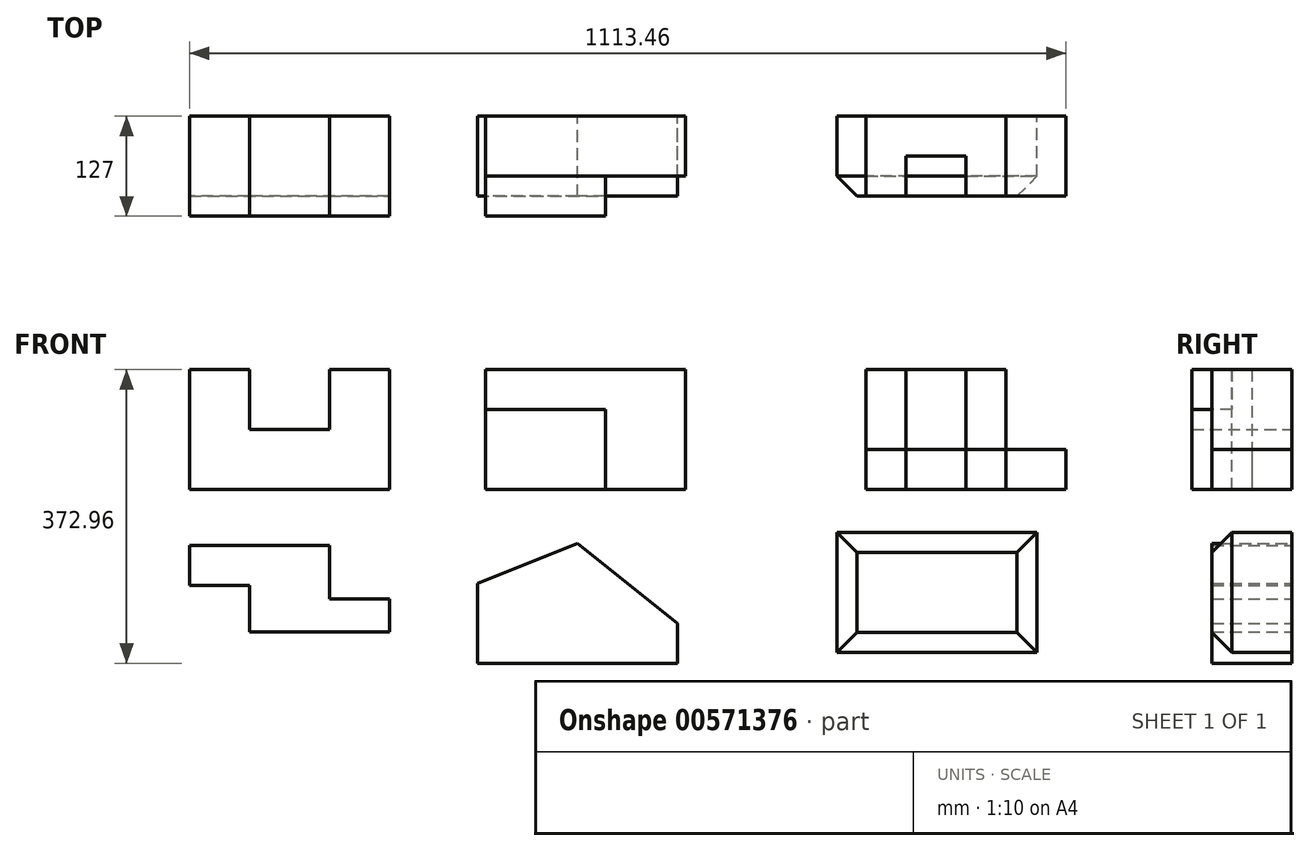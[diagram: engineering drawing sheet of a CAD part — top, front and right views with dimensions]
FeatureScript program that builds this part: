
annotation { "Feature Type Name" : "Feature", "Feature Type Description" : "" }
export const myFeature = defineFeature(function(context is Context, id is Id, definition is map)
    precondition{}
    {
        {
            var Q0;
            Q0=qCreatedBy(makeId("Front.planeOp"),FACE);
            var sketch = newSketch(context, id + "F0", { "sketchPlane" : qUnion([Q0])});
            skLineSegment(sketch, "E0", {"start": v(0, 0) * mm, "end": v(254, 0) * mm});
            skLineSegment(sketch, "E1", {"start": v(254, 0) * mm, "end": v(254, 152.4) * mm});
            skLineSegment(sketch, "E2", {"start": v(254, 152.4) * mm, "end": v(177.8, 152.4) * mm});
            skLineSegment(sketch, "E3", {"start": v(177.8, 152.4) * mm, "end": v(177.8, 76.2) * mm});
            skLineSegment(sketch, "E4", {"start": v(177.8, 76.2) * mm, "end": v(76.2, 76.2) * mm});
            skLineSegment(sketch, "E5", {"start": v(76.2, 76.2) * mm, "end": v(76.2, 152.4) * mm});
            skLineSegment(sketch, "E6", {"start": v(76.2, 152.4) * mm, "end": v(0, 152.4) * mm});
            skLineSegment(sketch, "E7", {"start": v(0, 152.4) * mm, "end": v(0, 0) * mm});
            skSolve(sketch);
        }
        {
            var Q0;
            Q0=makeQuery(id+"F0.imprint","IMPRINT",FACE,{"disambiguationData":[TD([[makeQuery(id+"F0.imprint","IMPRINT",EDGE,{"derivedFrom":sQuery(id+"F0.wireOp",EDGE,"E0")}),1.0]])]});
            var sketch = newSketch(context, id + "F1", { "sketchPlane" : qUnion([Q0])});
            skSolve(sketch);
        }
        {
            var Q0;
            Q0=makeQuery(id+"F1.imprint","IMPRINT",FACE,{"disambiguationData":[TD([[makeQuery(id+"F1.imprint","IMPRINT",EDGE,{"derivedFrom":makeQuery(id+"F0.imprint","IMPRINT",EDGE,{"derivedFrom":sQuery(id+"F0.wireOp",EDGE,"E0")})}),1.0]])]});
            extrude(context, id + "F2", {"entities" : qUnion([Q0]), "depth" : 25.4 * mm, "offsetDistance" : 25.4 * mm});
        }
        {
            var Q0;
            Q0=qCreatedBy(makeId("Front.planeOp"),FACE);
            var sketch = newSketch(context, id + "F3", { "sketchPlane" : qUnion([Q0])});
            skLineSegment(sketch, "E8", {"start": v(376.13, 0) * mm, "end": v(630.13, 0) * mm});
            skLineSegment(sketch, "E9", {"start": v(630.13, 0) * mm, "end": v(630.13, 152.4) * mm});
            skLineSegment(sketch, "E10", {"start": v(630.13, 152.4) * mm, "end": v(376.13, 152.4) * mm});
            skLineSegment(sketch, "E11", {"start": v(376.13, 152.4) * mm, "end": v(376.13, 0) * mm});
            skSolve(sketch);
        }
        {
            var Q0;
            Q0=makeQuery(id+"F3.imprint","IMPRINT",FACE,{"disambiguationData":[TD([[makeQuery(id+"F3.imprint","IMPRINT",EDGE,{"derivedFrom":sQuery(id+"F3.wireOp",EDGE,"E8")}),1.0]])]});
            extrude(context, id + "F4", {"entities" : qUnion([Q0]), "depth" : 25.4 * mm, "offsetDistance" : 25.4 * mm});
        }
        {
            var Q0;
            Q0=makeQuery(id+"F2.opExtrude","CAP_FACE",FACE,{"disambiguationData":[OSD([sQuery(id+"F0.wireOp",EDGE,"E0"),sQuery(id+"F0.wireOp",EDGE,"E1"),sQuery(id+"F0.wireOp",EDGE,"E2"),sQuery(id+"F0.wireOp",EDGE,"E3"),sQuery(id+"F0.wireOp",EDGE,"E4"),sQuery(id+"F0.wireOp",EDGE,"E5"),sQuery(id+"F0.wireOp",EDGE,"E6"),sQuery(id+"F0.wireOp",EDGE,"E7")])],"isStart":false});
            extrude(context, id + "F5", {"entities" : qUnion([Q0]), "operationType" : NewBodyOperationType.ADD, "depth" : 101.6 * mm, "offsetDistance" : 25.4 * mm});
        }
        {
            var Q0;
            Q0=makeQuery(id+"F4.opExtrude","CAP_FACE",FACE,{"disambiguationData":[OSD([sQuery(id+"F3.wireOp",EDGE,"E8"),sQuery(id+"F3.wireOp",EDGE,"E9"),sQuery(id+"F3.wireOp",EDGE,"E10"),sQuery(id+"F3.wireOp",EDGE,"E11")])],"isStart":false});
            extrude(context, id + "F6", {"entities" : qUnion([Q0]), "operationType" : NewBodyOperationType.ADD, "depth" : 101.6 * mm, "offsetDistance" : 25.4 * mm});
        }
        {
            var Q0;
            {var subQ0=sQuery(id+"F3.wireOp",EDGE,"E10");Q0=makeQuery(id+"F6.boolean.opBoolean","MERGE",FACE,{"derivedFrom":[makeQuery(id+"F4.opExtrude","SWEPT_FACE",FACE,{"disambiguationData":[OSD([subQ0])]}),makeQuery(id+"F6.opExtrude","SWEPT_FACE",FACE,{"disambiguationData":[OSD([subQ0])]})]});}
            var sketch = newSketch(context, id + "F7", { "sketchPlane" : qUnion([Q0])});
            skLineSegment(sketch, "E12", {"start": v(630.13, -127) * mm, "end": v(528.53, -127) * mm});
            skLineSegment(sketch, "E13", {"start": v(528.53, -127) * mm, "end": v(528.53, -76.2) * mm});
            skLineSegment(sketch, "E14", {"start": v(528.53, -76.2) * mm, "end": v(630.13, -76.2) * mm});
            skSolve(sketch);
        }
        {
            var Q0;
            {var subQ0=sQuery(id+"F7.wireOp",EDGE,"E12");Q0=makeQuery(id+"F7.imprint","IMPRINT",FACE,{"disambiguationData":[TD([[makeQuery(id+"F7.imprint","IMPRINT",EDGE,{"derivedFrom":subQ0}),-1.0]])]});}
            extrude(context, id + "F8", {"entities" : qUnion([Q0]), "operationType" : NewBodyOperationType.REMOVE, "oppositeDirection" : true, "depth" : 152.4 * mm, "offsetDistance" : 25.4 * mm});
        }
        {
            var Q0;
            Q0=makeQuery(id+"F6.opExtrude","CAP_FACE",FACE,{"disambiguationData":[OSD([sQuery(id+"F3.wireOp",EDGE,"E8"),sQuery(id+"F3.wireOp",EDGE,"E9"),sQuery(id+"F3.wireOp",EDGE,"E10"),sQuery(id+"F3.wireOp",EDGE,"E11")])],"isStart":false});
            var sketch = newSketch(context, id + "F9", { "sketchPlane" : qUnion([Q0])});
            skLineSegment(sketch, "E15", {"start": v(376.13, 152.4) * mm, "end": v(376.13, 101.6) * mm});
            skLineSegment(sketch, "E16", {"start": v(376.13, 101.6) * mm, "end": v(528.53, 101.6) * mm});
            skLineSegment(sketch, "E17", {"start": v(528.53, 101.6) * mm, "end": v(528.53, 152.4) * mm});
            skSolve(sketch);
        }
        {
            var Q0;
            Q0=makeQuery(id+"F9.imprint","IMPRINT",FACE,{"disambiguationData":[TD([[makeQuery(id+"F9.imprint","IMPRINT",EDGE,{"derivedFrom":sQuery(id+"F9.wireOp",EDGE,"E15")}),1.0]])]});
            extrude(context, id + "F10", {"entities" : qUnion([Q0]), "operationType" : NewBodyOperationType.REMOVE, "oppositeDirection" : true, "depth" : 50.8 * mm, "offsetDistance" : 25.4 * mm});
        }
        {
            var Q0;
            Q0=qCreatedBy(makeId("Top.planeOp"),FACE);
            var sketch = newSketch(context, id + "F11", { "sketchPlane" : qUnion([Q0])});
            skLineSegment(sketch, "E18", {"start": v(859.46, 0) * mm, "end": v(859.46, -101.6) * mm});
            skLineSegment(sketch, "E19", {"start": v(859.46, -101.6) * mm, "end": v(910.26, -101.6) * mm});
            skLineSegment(sketch, "E20", {"start": v(910.26, -101.6) * mm, "end": v(910.26, -50.8) * mm});
            skLineSegment(sketch, "E21", {"start": v(910.26, -50.8) * mm, "end": v(986.46, -50.8) * mm});
            skLineSegment(sketch, "E22", {"start": v(986.46, -50.8) * mm, "end": v(986.46, -101.6) * mm});
            skLineSegment(sketch, "E23", {"start": v(986.46, -101.6) * mm, "end": v(1113.46, -101.6) * mm});
            skLineSegment(sketch, "E24", {"start": v(1113.46, -101.6) * mm, "end": v(1113.46, 0) * mm});
            skLineSegment(sketch, "E25", {"start": v(1113.46, 0) * mm, "end": v(859.46, 0) * mm});
            skLineSegment(sketch, "E26", {"start": v(1037.26, 0) * mm, "end": v(1037.26, -101.6) * mm});
            skPoint(sketch, "E26.endSnap0", {"position": v(1049.96, -101.6) * mm});
            skSolve(sketch);
        }
        {
            var Q0;
            {var subQ0=sQuery(id+"F11.wireOp",EDGE,"E18");Q0=makeQuery(id+"F11.imprint","IMPRINT",FACE,{"disambiguationData":[TD([[makeQuery(id+"F11.imprint","IMPRINT",EDGE,{"derivedFrom":subQ0}),1.0]])]});}
            extrude(context, id + "F12", {"entities" : qUnion([Q0]), "depth" : 152.4 * mm, "offsetDistance" : 25.4 * mm});
        }
        {
            var Q0;
            Q0 = qSketchRegion(id + "F11", true);
            extrude(context, id + "F13", {"entities" : qUnion([Q0]), "depth" : 50.8 * mm, "offsetDistance" : 25.4 * mm});
        }
        {
            var Q0;
            Q0=qCreatedBy(makeId("Front.planeOp"),FACE);
            var sketch = newSketch(context, id + "F14", { "sketchPlane" : qUnion([Q0])});
            skLineSegment(sketch, "E27", {"start": v(0, -71.04) * mm, "end": v(0, -71.04) * mm});
            skLineSegment(sketch, "E28", {"start": v(0, -71.04) * mm, "end": v(177.8, -71.04) * mm});
            skLineSegment(sketch, "E29", {"start": v(177.8, -71.04) * mm, "end": v(177.8, -139.09) * mm});
            skLineSegment(sketch, "E30", {"start": v(177.8, -139.09) * mm, "end": v(254, -139.09) * mm});
            skLineSegment(sketch, "E31", {"start": v(254, -139.09) * mm, "end": v(254, -180.75) * mm});
            skLineSegment(sketch, "E32", {"start": v(254, -180.75) * mm, "end": v(76.2, -180.75) * mm});
            skLineSegment(sketch, "E33", {"start": v(76.2, -180.75) * mm, "end": v(76.2, -121.84) * mm});
            skLineSegment(sketch, "E34", {"start": v(76.2, -121.84) * mm, "end": v(0, -121.84) * mm});
            skLineSegment(sketch, "E35", {"start": v(0, -121.84) * mm, "end": v(0, -71.04) * mm});
            skSolve(sketch);
        }
        {
            var Q0;
            Q0=makeQuery(id+"F14.imprint","IMPRINT",FACE,{"disambiguationData":[TD([[makeQuery(id+"F14.imprint","IMPRINT",EDGE,{"derivedFrom":sQuery(id+"F14.wireOp",EDGE,"E28")}),-1.0]])]});
            extrude(context, id + "F15", {"entities" : qUnion([Q0]), "depth" : 101.6 * mm, "offsetDistance" : 25.4 * mm});
        }
        {
            var Q0;
            Q0=qCreatedBy(makeId("Front.planeOp"),FACE);
            var sketch = newSketch(context, id + "F16", { "sketchPlane" : qUnion([Q0])});
            skLineSegment(sketch, "E36", {"start": v(365.7, -220.56) * mm, "end": v(619.7, -220.56) * mm});
            skLineSegment(sketch, "E37", {"start": v(619.7, -220.56) * mm, "end": v(619.7, -169.76) * mm});
            skLineSegment(sketch, "E38", {"start": v(619.7, -169.76) * mm, "end": v(492.7, -68.16) * mm});
            skLineSegment(sketch, "E39", {"start": v(492.7, -68.16) * mm, "end": v(365.7, -118.96) * mm});
            skLineSegment(sketch, "E40", {"start": v(365.7, -118.96) * mm, "end": v(365.7, -220.56) * mm});
            skSolve(sketch);
        }
        {
            var Q0;
            Q0=makeQuery(id+"F16.imprint","IMPRINT",FACE,{"disambiguationData":[TD([[makeQuery(id+"F16.imprint","IMPRINT",EDGE,{"derivedFrom":sQuery(id+"F16.wireOp",EDGE,"E36")}),1.0]])]});
            extrude(context, id + "F17", {"entities" : qUnion([Q0]), "depth" : 101.6 * mm, "offsetDistance" : 25.4 * mm});
        }
        {
            var Q0;
            Q0=qCreatedBy(makeId("Front.planeOp"),FACE);
            var sketch = newSketch(context, id + "F18", { "sketchPlane" : qUnion([Q0])});
            skLineSegment(sketch, "E41", {"start": v(822.42, -206.9) * mm, "end": v(1076.42, -206.9) * mm});
            skLineSegment(sketch, "E42", {"start": v(822.42, -206.9) * mm, "end": v(822.42, -54.5) * mm});
            skLineSegment(sketch, "E43", {"start": v(822.42, -54.5) * mm, "end": v(1076.42, -54.5) * mm});
            skLineSegment(sketch, "E44", {"start": v(1076.42, -54.5) * mm, "end": v(1076.42, -206.9) * mm});
            skSolve(sketch);
        }
        {
            var Q0;
            Q0=makeQuery(id+"F18.imprint","IMPRINT",FACE,{"disambiguationData":[TD([[makeQuery(id+"F18.imprint","IMPRINT",EDGE,{"derivedFrom":sQuery(id+"F18.wireOp",EDGE,"E41")}),1.0]])]});
            extrude(context, id + "F19", {"entities" : qUnion([Q0]), "depth" : 101.6 * mm, "offsetDistance" : 25.4 * mm});
        }
        {
            var Q0;
            Q0=makeQuery(id+"F19.opExtrude","CAP_FACE",FACE,{"disambiguationData":[OSD([sQuery(id+"F18.wireOp",EDGE,"E41"),sQuery(id+"F18.wireOp",EDGE,"E42"),sQuery(id+"F18.wireOp",EDGE,"E43"),sQuery(id+"F18.wireOp",EDGE,"E44")])],"isStart":false});
            chamfer(context, id + "F20", {"entities" : qUnion([Q0]), "width" : 25.4 * mm, "tangentPropagation" : true});
        }
    });
